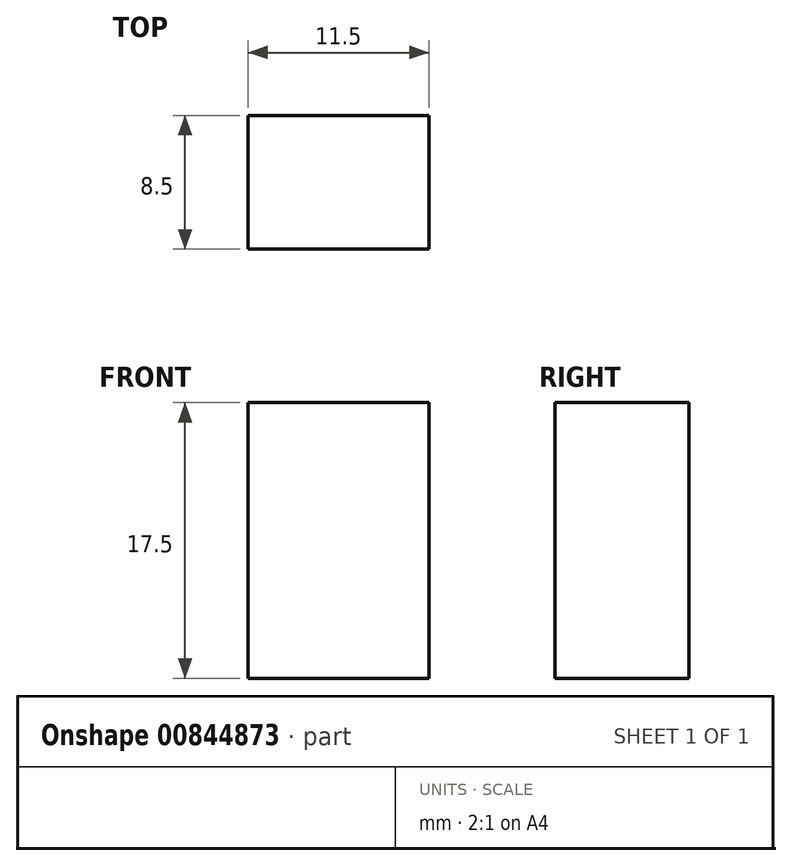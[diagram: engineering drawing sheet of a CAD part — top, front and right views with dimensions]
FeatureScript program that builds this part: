
annotation { "Feature Type Name" : "Feature", "Feature Type Description" : "" }
export const myFeature = defineFeature(function(context is Context, id is Id, definition is map)
    precondition{}
    {
        {
            var Q0;
            Q0=qCreatedBy(makeId("Front.planeOp"),FACE);
            var sketch = newSketch(context, id + "F0", { "sketchPlane" : qUnion([Q0])});
            skLineSegment(sketch, "E0.bottom", {"start": v(-5.75, -8.75) * mm, "end": v(5.75, -8.75) * mm});
            skLineSegment(sketch, "E0.top", {"start": v(-5.75, 8.75) * mm, "end": v(5.75, 8.75) * mm});
            skLineSegment(sketch, "E0.left", {"start": v(-5.75, -8.75) * mm, "end": v(-5.75, 8.75) * mm});
            skLineSegment(sketch, "E0.right", {"start": v(5.75, -8.75) * mm, "end": v(5.75, 8.75) * mm});
            skPoint(sketch, "E0.middle", {"position": v(0, 0) * mm});
            skSolve(sketch);
        }
        {
            var Q0;
            Q0 = qSketchRegion(id + "F0", true);
            extrude(context, id + "F1", {"entities" : qUnion([Q0]), "oppositeDirection" : true, "depth" : 8.5 * mm, "offsetDistance" : 25 * mm});
        }
        {
            var Q0;
            Q0=makeQuery(id+"F1.opExtrude","SWEPT_FACE",FACE,{"disambiguationData":[OSD([sQuery(id+"F0.wireOp",EDGE,"E0.bottom")])]});
            var sketch = newSketch(context, id + "F2", { "sketchPlane" : qUnion([Q0])});
            skPoint(sketch, "E1.centerSnap0", {"position": v(-5.75, -4.25) * mm});
            skLineSegment(sketch, "E2", {"start": v(-6.56, -6.5) * mm, "end": v(6.95, -6.5) * mm});
            skCircle(sketch, "E3", {"center": v(0, -6.5) * mm, "radius": 0.5 * mm});
            skCircle(sketch, "E4", {"center": v(-2.54, -6.5) * mm, "radius": 0.5 * mm});
            skCircle(sketch, "E5.MirrorC", {"center": v(2.54, -6.5) * mm, "radius": 0.5 * mm});
            skSolve(sketch);
        }
        {
            var Q0;
            Q0=sQuery(id+"F2.wireOp",EDGE,"E4");
            var Q1;
            Q1=sQuery(id+"F2.wireOp",EDGE,"E3");
            var Q2;
            Q2=sQuery(id+"F2.wireOp",EDGE,"E5.MirrorC");
            extrude(context, id + "F3", {"bodyType" : ToolBodyType.SURFACE, "surfaceEntities" : qUnion([Q0, Q1, Q2]), "depth" : 5 * mm, "offsetDistance" : 25 * mm});
        }
    });
